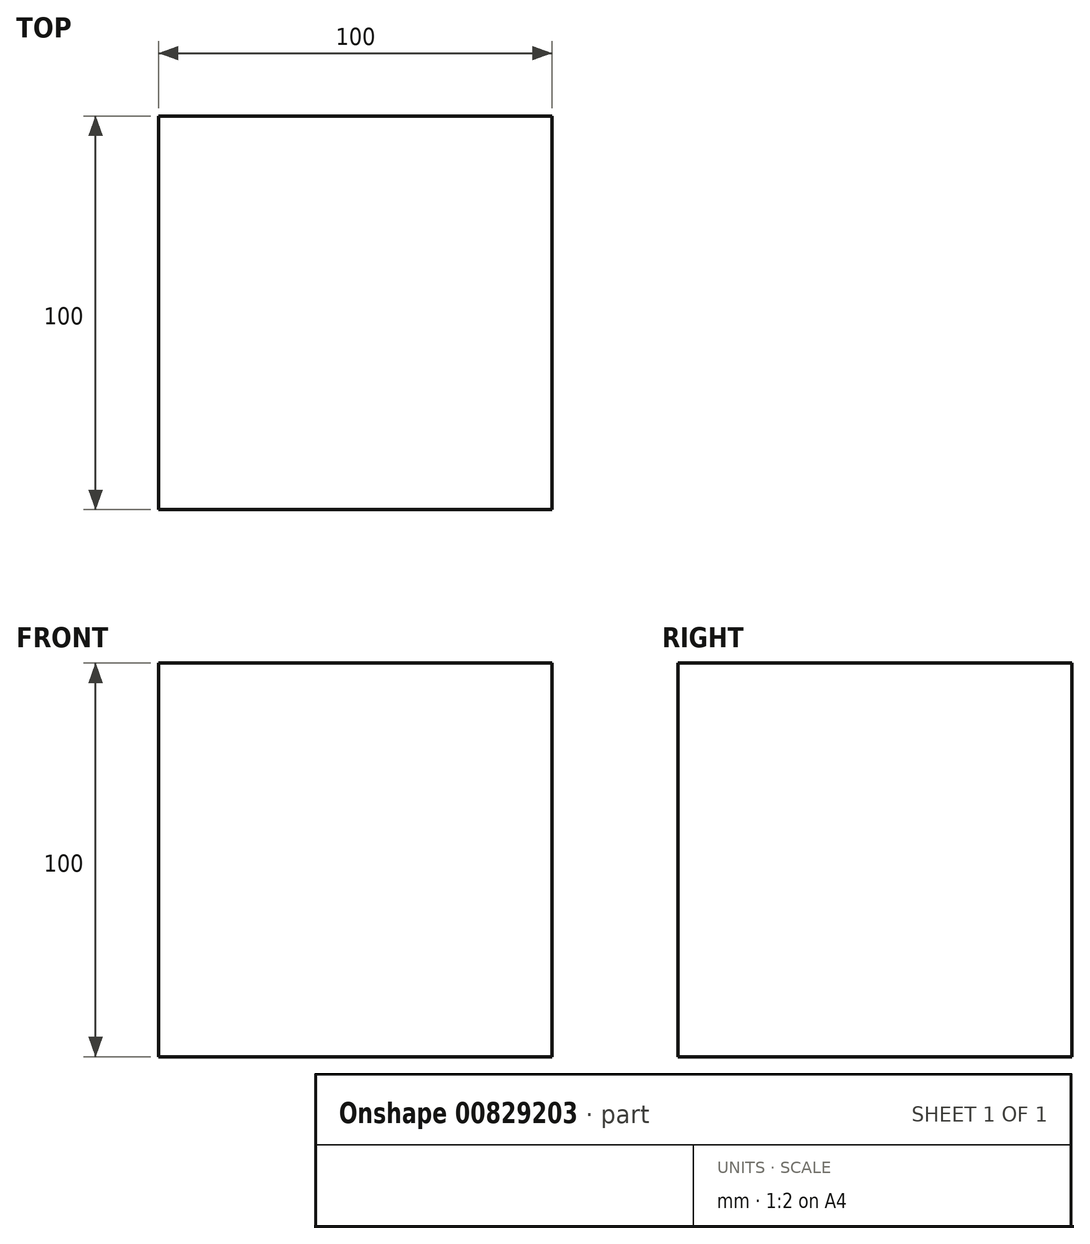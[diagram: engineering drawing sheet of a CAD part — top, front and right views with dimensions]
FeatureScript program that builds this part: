
annotation { "Feature Type Name" : "Feature", "Feature Type Description" : "" }
export const myFeature = defineFeature(function(context is Context, id is Id, definition is map)
    precondition{}
    {
        {
            var Q0;
            Q0=qCreatedBy(makeId("Top.planeOp"),FACE);
            var sketch = newSketch(context, id + "F0", { "sketchPlane" : qUnion([Q0])});
            skLineSegment(sketch, "E0.bottom", {"start": v(-50, 50) * mm, "end": v(50, 50) * mm});
            skLineSegment(sketch, "E0.top", {"start": v(-50, -50) * mm, "end": v(50, -50) * mm});
            skLineSegment(sketch, "E0.left", {"start": v(-50, 50) * mm, "end": v(-50, -50) * mm});
            skLineSegment(sketch, "E0.right", {"start": v(50, 50) * mm, "end": v(50, -50) * mm});
            skPoint(sketch, "E0.middle", {"position": v(0, 0) * mm});
            skLineSegment(sketch, "E1.bottom", {"start": v(50, -9.56) * mm, "end": v(50, -9.56) * mm});
            skLineSegment(sketch, "E1.top", {"start": v(50, 9.56) * mm, "end": v(50, 9.56) * mm});
            skLineSegment(sketch, "E1.left", {"start": v(50, -9.56) * mm, "end": v(50, 9.56) * mm});
            skLineSegment(sketch, "E1.right", {"start": v(50, -9.56) * mm, "end": v(50, 9.56) * mm});
            skPoint(sketch, "E1.middle", {"position": v(50, 0) * mm});
            skSolve(sketch);
        }
        {
            var Q0;
            Q0 = qSketchRegion(id + "F0", true);
            extrude(context, id + "F1", {"entities" : qUnion([Q0]), "depth" : 100 * mm, "offsetDistance" : 25 * mm});
        }
    });
